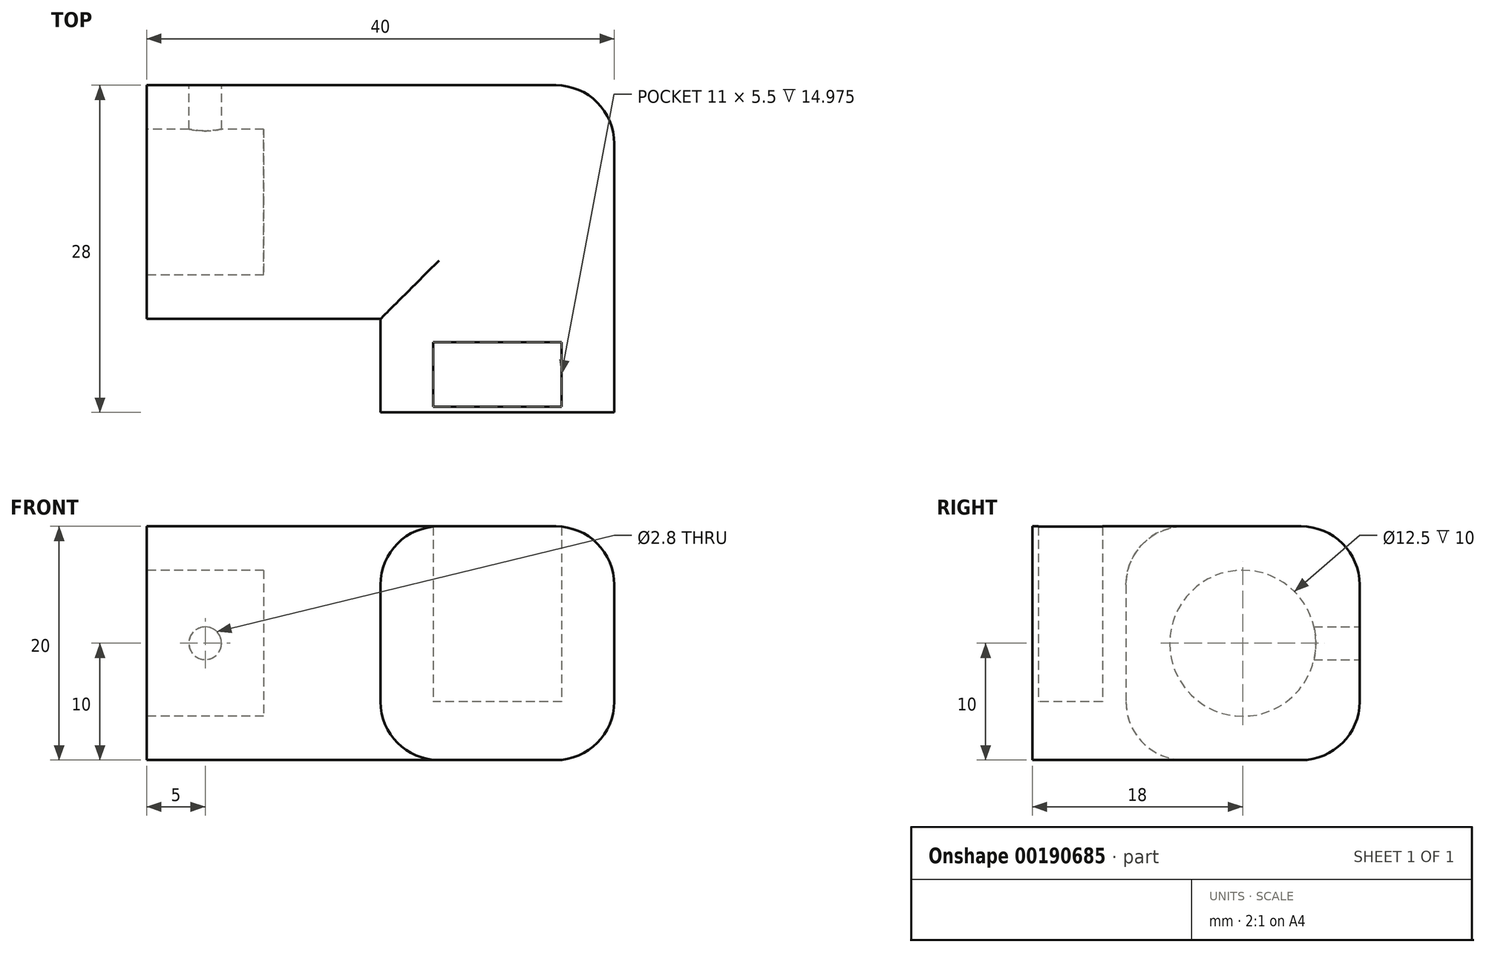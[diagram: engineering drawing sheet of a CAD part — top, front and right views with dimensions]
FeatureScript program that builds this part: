
annotation { "Feature Type Name" : "Feature", "Feature Type Description" : "" }
export const myFeature = defineFeature(function(context is Context, id is Id, definition is map)
    precondition{}
    {
        {
            var Q0;
            Q0=qCreatedBy(makeId("Top.planeOp"),FACE);
            var sketch = newSketch(context, id + "F0", { "sketchPlane" : qUnion([Q0])});
            skLineSegment(sketch, "E0", {"start": v(0, 0) * mm, "end": v(30, 0) * mm, "construction": true});
            skLineSegment(sketch, "E1", {"start": v(30, 0) * mm, "end": v(30, -18) * mm, "construction": true});
            skLineSegment(sketch, "E2", {"start": v(0, 0) * mm, "end": v(0, -10) * mm});
            skLineSegment(sketch, "E3", {"start": v(0, -10) * mm, "end": v(20, -10) * mm});
            skLineSegment(sketch, "E4", {"start": v(20, -10) * mm, "end": v(20, -18) * mm});
            skLineSegment(sketch, "E5", {"start": v(20, -18) * mm, "end": v(40, -18) * mm});
            skLineSegment(sketch, "E6", {"start": v(40, -18) * mm, "end": v(40, 10) * mm});
            skLineSegment(sketch, "E7", {"start": v(40, 10) * mm, "end": v(0, 10) * mm});
            skLineSegment(sketch, "E8", {"start": v(0, 10) * mm, "end": v(0, -10) * mm});
            skLineSegment(sketch, "E9", {"start": v(35.5, -17.5) * mm, "end": v(30, -17.5) * mm});
            skLineSegment(sketch, "E10", {"start": v(30, -17.5) * mm, "end": v(24.5, -17.5) * mm});
            skLineSegment(sketch, "E11", {"start": v(24.5, -17.5) * mm, "end": v(24.5, -12) * mm});
            skLineSegment(sketch, "E12", {"start": v(24.5, -12) * mm, "end": v(35.5, -12) * mm});
            skLineSegment(sketch, "E13", {"start": v(35.5, -12) * mm, "end": v(35.5, -17.5) * mm});
            skSolve(sketch);
        }
        {
            var Q0;
            {var subQ1=sQuery(id+"F0.wireOp",EDGE,"E3");Q0=makeQuery(id+"F0.imprint","IMPRINT",FACE,{"disambiguationData":[TD([[makeQuery(id+"F0.imprint","IMPRINT",EDGE,{"derivedFrom":subQ1}),1.0]])]});}
            extrude(context, id + "F1", {"entities" : qUnion([Q0]), "depth" : 20 * mm, "offsetDistance" : 25 * mm});
        }
        {
            var Q0;
            Q0=makeQuery(id+"F0.imprint","IMPRINT",FACE,{"disambiguationData":[TD([[makeQuery(id+"F0.imprint","IMPRINT",EDGE,{"derivedFrom":sQuery(id+"F0.wireOp",EDGE,"E9")}),-1.0]])]});
            extrude(context, id + "F2", {"entities" : qUnion([Q0]), "operationType" : NewBodyOperationType.ADD, "depth" : 5 * mm, "offsetDistance" : 25 * mm});
        }
        {
            var Q0;
            Q0=makeQuery(id+"F1.opExtrude","SWEPT_FACE",FACE,{"disambiguationData":[OSD([sQuery(id+"F0.wireOp",EDGE,"E8")])]});
            var sketch = newSketch(context, id + "F3", { "sketchPlane" : qUnion([Q0])});
            skPoint(sketch, "E14", {"position": v(0, 10) * mm});
            skPoint(sketch, "E14.positionSnap0", {"position": v(10, 10) * mm});
            skCircle(sketch, "E15", {"center": v(0, 10) * mm, "radius": 6.25 * mm});
            skSolve(sketch);
        }
        {
            var Q0;
            Q0=makeQuery(id+"F3.imprint","IMPRINT",FACE,{"disambiguationData":[TD([[makeQuery(id+"F3.imprint","IMPRINT",EDGE,{"derivedFrom":sQuery(id+"F3.wireOp",EDGE,"E15")}),1.0]])]});
            var Q1;
            Q1=sQuery(id+"F3.wireOp",EDGE,"E15");
            extrude(context, id + "F4", {"entities" : qUnion([Q0]), "operationType" : NewBodyOperationType.REMOVE, "surfaceOperationType" : NewSurfaceOperationType.ADD, "surfaceEntities" : qUnion([Q1]), "oppositeDirection" : true, "depth" : 10 * mm, "offsetDistance" : 25 * mm});
        }
        {
            var Q0;
            Q0=makeQuery(id+"F1.opExtrude","SWEPT_FACE",FACE,{"disambiguationData":[OSD([sQuery(id+"F0.wireOp",EDGE,"E7")])]});
            var sketch = newSketch(context, id + "F5", { "sketchPlane" : qUnion([Q0])});
            skLineSegment(sketch, "E16", {"start": v(0, 10) * mm, "end": v(-5, 10) * mm, "construction": true});
            skCircle(sketch, "E17", {"center": v(-5, 10) * mm, "radius": 1.4 * mm});
            skSolve(sketch);
        }
        {
            var Q0;
            Q0=makeQuery(id+"F5.imprint","IMPRINT",FACE,{"disambiguationData":[TD([[makeQuery(id+"F5.imprint","IMPRINT",EDGE,{"derivedFrom":sQuery(id+"F5.wireOp",EDGE,"E17")}),1.0]])]});
            extrude(context, id + "F6", {"entities" : qUnion([Q0]), "operationType" : NewBodyOperationType.REMOVE, "endBound" : BoundingType.UP_TO_NEXT, "oppositeDirection" : true, "depth" : 25 * mm, "offsetDistance" : 25 * mm});
        }
        {
            var Q0;
            Q0=makeQuery(id+"F1.opExtrude","CAP_EDGE",EDGE,{"disambiguationData":[OSD([sQuery(id+"F0.wireOp",EDGE,"E7")])],"isStart":false});
            var Q1;
            Q1=makeQuery(id+"F1.opExtrude","CAP_EDGE",EDGE,{"disambiguationData":[OSD([sQuery(id+"F0.wireOp",EDGE,"E7")])],"isStart":true});
            var Q2;
            Q2=makeQuery(id+"F1.opExtrude","CAP_EDGE",EDGE,{"disambiguationData":[OSD([sQuery(id+"F0.wireOp",EDGE,"E3")])],"isStart":false});
            var Q3;
            Q3=makeQuery(id+"F1.opExtrude","CAP_EDGE",EDGE,{"disambiguationData":[OSD([sQuery(id+"F0.wireOp",EDGE,"E3")])],"isStart":true});
            var Q4;
            Q4=makeQuery(id+"F1.opExtrude","CAP_EDGE",EDGE,{"disambiguationData":[OSD([sQuery(id+"F0.wireOp",EDGE,"E4")])],"isStart":false});
            var Q5;
            Q5=makeQuery(id+"F1.opExtrude","CAP_EDGE",EDGE,{"disambiguationData":[OSD([sQuery(id+"F0.wireOp",EDGE,"E4")])],"isStart":true});
            var Q6;
            Q6=makeQuery(id+"F1.opExtrude","CAP_EDGE",EDGE,{"disambiguationData":[OSD([sQuery(id+"F0.wireOp",EDGE,"E6")])],"isStart":false});
            var Q7;
            Q7=makeQuery(id+"F1.opExtrude","CAP_EDGE",EDGE,{"disambiguationData":[OSD([sQuery(id+"F0.wireOp",EDGE,"E6")])],"isStart":true});
            var Q8;
            Q8=makeQuery(id+"F1.opExtrude","SWEPT_EDGE",EDGE,{"disambiguationData":[OSD([sQuery(id+"F0.wireOp",EDGE,"E6"),sQuery(id+"F0.wireOp",EDGE,"E7")])]});
            fillet(context, id + "F7", {"entities" : qUnion([Q0, Q1, Q2, Q3, Q4, Q5, Q6, Q7, Q8]), "radius" : 5 * mm, "tangentPropagation" : true, "allowEdgeOverflow" : false});
        }
    });
